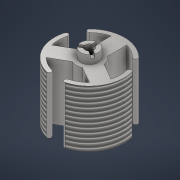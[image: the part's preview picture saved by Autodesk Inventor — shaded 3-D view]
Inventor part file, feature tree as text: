
AUTODESK INVENTOR PART (.ipt)
format: ipt  version: 2021 (Build 250183000, 183)  size: 263,680 bytes
history: native  units: mm
features: other x7, extrude x5, sketch x5, fillet x1, thread x1
ambient origin geometry x8: Origin, YZ Plane, XZ Plane, XY Plane, X Axis, Y Axis, Z Axis, Center Point
bodies: Body1 (feature_tree)
feature tree (19):
  other  "Suporte Bobinas"
  other  "Sólido1"
  extrude  "Extrusão1"  Depth=1.0mm
  extrude  "Extrusão2"  Depth=6.5mm TaperAngle=0.0deg
  fillet  "Arredondamento1"  Radius=30.0mm
  extrude  "Extrusão3"  Depth=30.0mm
  extrude  "Extrusão4"  Depth=6.5mm TaperAngle=0.0deg
  extrude  "Extrusão5"  Depth=0.5mm
  thread  "Rosca1"  [1 undecoded]
  sketch  "Esboço1"  dims[d0=1.0mm d1=2.0mm]
  sketch  "Esboço3"  dims[d2=3.0mm d3=6.5mm d4=0.0mm d7=30.0mm d9=360.0deg]
  other  "Contorno projetado1"
  sketch  "Esboço4"  dims[d11=7.0mm d16=30.0mm d17=0.75mm]
  sketch  "Esboço5"  dims[d19=30.0mm d21=360.0deg d23=6.5mm d24=0.0mm]
  other  "Contorno projetado2"
  sketch  "Esboço6"  dims[d25=0.25mm d26=2.0mm d27=1.0mm d28=7.5mm d29=0.0mm d30=0.0mm d33=30.0mm d35=360.0deg d37=0.4mm d38=0.0mm d39=0.4mm d40=0.2mm d41=0.4mm d42=0.0mm d43=6.5mm d44=0.0mm d5=0.5mm d6=0.872665mm]
  other  "Contorno projetado3"
  other  "Contorno projetado4"
  other  "Contorno projetado5"
note: 1 required parameter value undecoded (feature->parameter linkage not recoverable at this tier; creation-order binding heuristic only, values carry confidence <= 0.55)
